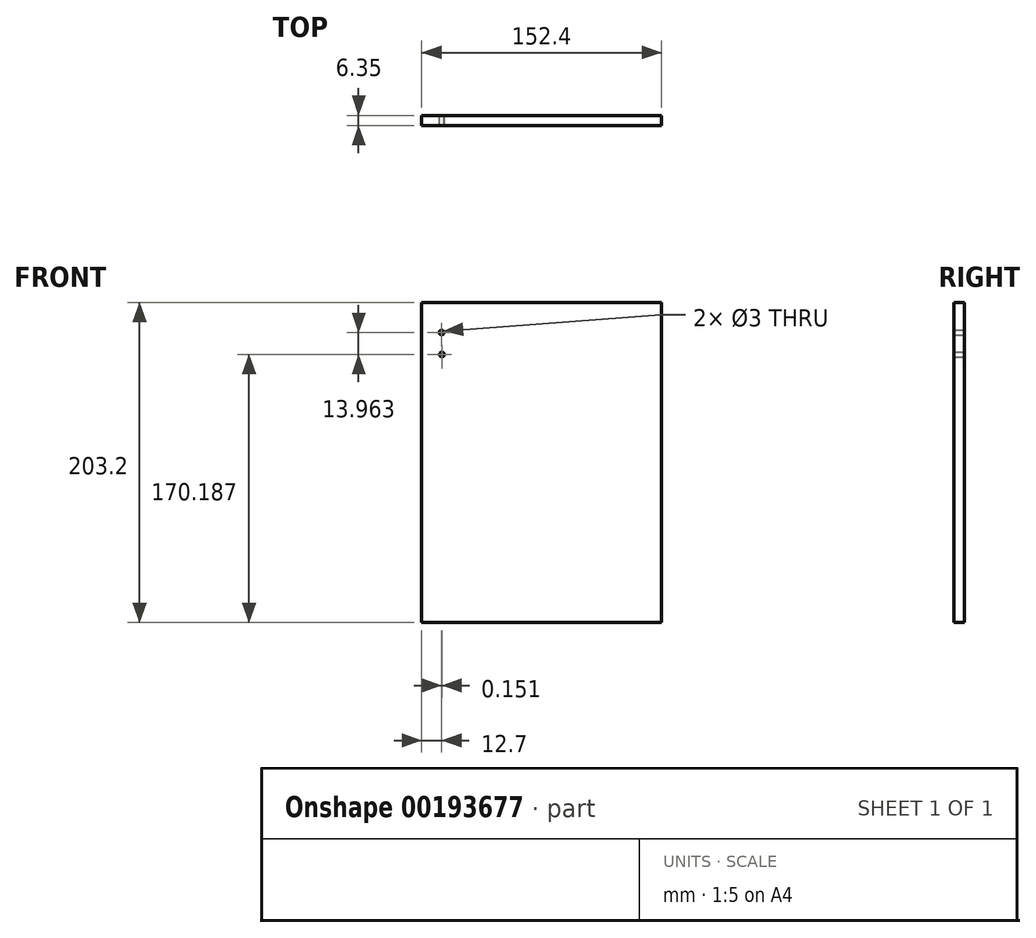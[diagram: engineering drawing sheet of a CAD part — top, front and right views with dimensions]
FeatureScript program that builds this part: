
annotation { "Feature Type Name" : "Feature", "Feature Type Description" : "" }
export const myFeature = defineFeature(function(context is Context, id is Id, definition is map)
    precondition{}
    {
        {
            var Q0;
            Q0=qCreatedBy(makeId("Front.planeOp"),FACE);
            var sketch = newSketch(context, id + "F0", { "sketchPlane" : qUnion([Q0])});
            skLineSegment(sketch, "E0.bottom", {"start": v(-76.2, 101.6) * mm, "end": v(76.2, 101.6) * mm});
            skLineSegment(sketch, "E0.top", {"start": v(-76.2, -101.6) * mm, "end": v(76.2, -101.6) * mm});
            skLineSegment(sketch, "E0.left", {"start": v(-76.2, 101.6) * mm, "end": v(-76.2, -101.6) * mm});
            skLineSegment(sketch, "E0.right", {"start": v(76.2, 101.6) * mm, "end": v(76.2, -101.6) * mm});
            skPoint(sketch, "E0.middle", {"position": v(0, 0) * mm});
            skSolve(sketch);
        }
        {
            var Q0;
            Q0=makeQuery(id+"F0.imprint","IMPRINT",FACE,{"disambiguationData":[TD([[makeQuery(id+"F0.imprint","IMPRINT",EDGE,{"derivedFrom":sQuery(id+"F0.wireOp",EDGE,"E0.bottom")}),-1.0]])]});
            extrude(context, id + "F1", {"entities" : qUnion([Q0]), "depth" : 6.35 * mm});
        }
        {
            var Q0;
            Q0=qCreatedBy(makeId("Front.planeOp"),FACE);
            var sketch = newSketch(context, id + "F2", { "sketchPlane" : qUnion([Q0])});
            skCircle(sketch, "E1", {"center": v(-63.5, 82.55) * mm, "radius": 1.5 * mm});
            skSolve(sketch);
        }
        {
            var Q0;
            Q0=qCreatedBy(makeId("Front.planeOp"),FACE);
            var sketch = newSketch(context, id + "F3", { "sketchPlane" : qUnion([Q0])});
            skCircle(sketch, "E2", {"center": v(-63.35, 68.59) * mm, "radius": 1.5 * mm});
            skSolve(sketch);
        }
        {
            var Q0;
            Q0=makeQuery(id+"F2.imprint","IMPRINT",FACE,{"disambiguationData":[TD([[makeQuery(id+"F2.imprint","IMPRINT",EDGE,{"derivedFrom":sQuery(id+"F2.wireOp",EDGE,"E1")}),1.0]])]});
            var Q1;
            Q1=makeQuery(id+"F3.imprint","IMPRINT",FACE,{"disambiguationData":[TD([[makeQuery(id+"F3.imprint","IMPRINT",EDGE,{"derivedFrom":sQuery(id+"F3.wireOp",EDGE,"E2")}),1.0]])]});
            extrude(context, id + "F4", {"entities" : qUnion([Q0, Q1]), "operationType" : NewBodyOperationType.REMOVE, "depth" : 25.4 * mm});
        }
    });
